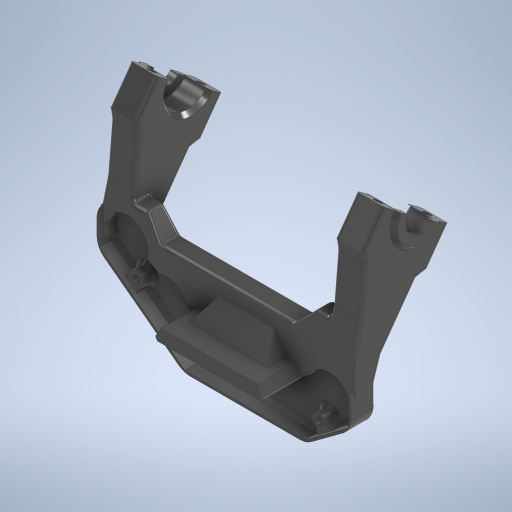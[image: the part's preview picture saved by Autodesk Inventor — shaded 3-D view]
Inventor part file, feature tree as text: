
AUTODESK INVENTOR PART (.ipt)
format: ipt  version: 2023.4 (Build 274418000, 418)  size: 1,474,048 bytes
history: native  units: mm
features: extrude x28, sketch x28, projected_geometry x26, chamfer x11, fillet x11, thicken_offset x4, mirror x1
ambient origin geometry x8: Origin, YZ Plane, XZ Plane, XY Plane, X Axis, Y Axis, Z Axis, Center Point
bodies: Solid1 (feature_tree)
feature tree (109):
  extrude  "Extrusion1"  Depth=10.0mm TaperAngle=0.0deg
  extrude  "Extrusion2"  Depth=6.0mm TaperAngle=0.0deg
  extrude  "Extrusion3"  Depth=4.3mm
  extrude  "Extrusion4"  Depth=4.3mm
  extrude  "Extrusion5"  Depth=10.0mm
  extrude  "Extrusion6"  Depth=7.2mm
  extrude  "Extrusion7"  Depth=3.3mm TaperAngle=0.0deg
  extrude  "Extrusion8"  Depth=10.0mm
  extrude  "Extrusion9"  Depth=2.0mm TaperAngle=45.0deg
  thicken_offset  "Thicken1"
  chamfer  "Chamfer1"  Distance=2.0mm Angle=45.0deg
  chamfer  "Chamfer2"  Distance=2.0mm Angle=45.0deg
  chamfer  "Chamfer3"  Distance=15.0mm
  thicken_offset  "Thicken2"
  mirror  "Mirror1"
  extrude  "Extrusion16"  Depth=15.0mm TaperAngle=0.0deg
  extrude  "Extrusion17"  Depth=10.0mm TaperAngle=0.0deg
  extrude  "Extrusion18"  TaperAngle=0.0deg  [1 undecoded]
  extrude  "Extrusion19"  TaperAngle=0.0deg  [1 undecoded]
  extrude  "Extrusion20"  Depth=10.0mm TaperAngle=0.0deg
  chamfer  "Chamfer7"  [1 undecoded]
  extrude  "Extrusion22"  Depth=4.3mm
  extrude  "Extrusion23"  Depth=4.3mm
  extrude  "Extrusion24"  Depth=7.5mm
  extrude  "Extrusion25"  Depth=7.5mm
  extrude  "Extrusion26"  Depth=3.5mm
  extrude  "Extrusion27"  Depth=7.5mm
  extrude  "Extrusion28"  Depth=15.0mm TaperAngle=0.0deg
  extrude  "Extrusion29"  Depth=10.0mm TaperAngle=0.0deg
  extrude  "Extrusion30"  Depth=2.0mm TaperAngle=45.0deg
  extrude  "Extrusion31"  Depth=2.0mm TaperAngle=45.0deg
  chamfer  "Chamfer8"  Distance=2.0mm
  chamfer  "Chamfer9"  Distance=2.0mm
  fillet  "Fillet1"  Radius=2.0mm
  fillet  "Fillet2"  Radius=2.0mm
  fillet  "Fillet3"  Radius=2.0mm
  fillet  "Fillet4"  Radius=2.0mm
  fillet  "Fillet5"  Radius=2.0mm
  fillet  "Fillet6"  Radius=2.0mm
  fillet  "Fillet7"  Radius=2.0mm
  fillet  "Fillet8"  Radius=2.0mm
  fillet  "Fillet9"  Radius=2.0mm
  fillet  "Fillet10"  Radius=16.0mm
  fillet  "Fillet11"  Radius=4.0mm
  extrude  "Extrusion32"  Depth=2.0mm TaperAngle=45.0deg
  chamfer  "Chamfer11"  Distance=4.0mm
  extrude  "Extrusion33"  Depth=2.0mm TaperAngle=45.0deg
  chamfer  "Chamfer12"  Distance=0.5mm
  extrude  "Extrusion34"  Depth=2.0mm TaperAngle=0.0deg
  extrude  "Extrusion36"  Depth=2.0mm TaperAngle=45.0deg
  chamfer  "Chamfer13"  Distance=5.0mm
  thicken_offset  "Thicken3"
  thicken_offset  "Thicken4"
  chamfer  "Chamfer14"  Distance=0.2mm
  chamfer  "Chamfer15"  Distance=0.2mm
  sketch  "Sketch1"  dims[d0=10.0mm d1=0.0mm d2=20.0mm d3=0.0mm]
  sketch  "Sketch2"  dims[d4=12.0mm d5=0.0mm d6=6.0mm d7=0.0mm]
  sketch  "Sketch5"  dims[d8=6.0mm d9=0.0mm d10=4.3mm]
  sketch  "Sketch6"  dims[d11=4.3mm d12=4.3mm]
  projected_geometry  "Projected Loop1"
  sketch  "Sketch7"  dims[d13=10.0mm d14=0.0mm d15=7.2mm]
  sketch  "Sketch8"  dims[d16=7.2mm d17=7.2mm]
  sketch  "Sketch9"  dims[d18=1.0mm d19=0.0mm d20=3.3mm d21=0.0mm]
  projected_geometry  "Projected Loop2"
  sketch  "Sketch10"  dims[d22=10.0mm d23=0.0mm d24=0.1mm]
  projected_geometry  "Projected Loop3"
  projected_geometry  "Projected Loop4"
  projected_geometry  "Projected Loop5"
  sketch  "Sketch11"  dims[d25=0.1mm d26=2.0mm d27=2.0mm d28=45.0deg d29=2.0mm d30=2.0mm d31=45.0deg d32=2.0mm d33=2.0mm d34=45.0deg]
  sketch  "Sketch18"  dims[d38=0.1mm]
  sketch  "Sketch19"  dims[d39=0.1mm]
  sketch  "Sketch20"  dims[d58=32.0mm]
  projected_geometry  "Projected Loop8"
  projected_geometry  "Projected Loop9"
  sketch  "Sketch21"  dims[d59=110.0mm]
  sketch  "Sketch22"  dims[d60=40.0mm d61=15.0mm d62=0.0mm]
  projected_geometry  "Projected Loop10"
  projected_geometry  "Projected Loop11"
  sketch  "Sketch24"  dims[d63=15.0mm d64=0.0mm d65=15.0mm d66=0.0mm]
  projected_geometry  "Projected Loop12"
  sketch  "Sketch25"  dims[d67=15.0mm d68=0.0mm d69=10.0mm d70=0.0mm]
  projected_geometry  "Projected Loop13"
  sketch  "Sketch26"  dims[d71=6.0mm d72=2.0mm d73=45.0deg d77=0.0mm d78=0.0mm]
  projected_geometry  "Projected Loop14"
  sketch  "Sketch27"  dims[d79=10.0mm d80=0.0mm d81=0.0mm d82=0.0mm]
  sketch  "Sketch28"  dims[d83=10.0mm d84=0.0mm d85=10.0mm d86=0.0mm]
  projected_geometry  "Projected Loop15"
  projected_geometry  "Projected Loop16"
  sketch  "Sketch29"  dims[d87=25.0mm d88=0.0mm d89=0.0mm]
  sketch  "Sketch30"  dims[d90=4.3mm d91=4.3mm]
  sketch  "Sketch32"  dims[d92=4.3mm d93=4.3mm]
  projected_geometry  "Projected Loop17"
  projected_geometry  "Projected Loop18"
  projected_geometry  "Projected Loop19"
  projected_geometry  "Projected Loop20"
  sketch  "Sketch33"  dims[d94=3.5mm d95=7.5mm]
  projected_geometry  "Projected Loop21"
  projected_geometry  "Projected Loop22"
  sketch  "Sketch34"  dims[d96=3.5mm d97=7.5mm]
  projected_geometry  "Projected Loop23"
  projected_geometry  "Projected Loop24"
  sketch  "Sketch35"  dims[d98=3.5mm d99=3.5mm]
  projected_geometry  "Projected Loop25"
  sketch  "Sketch36"  dims[d100=7.5mm d101=7.5mm]
  projected_geometry  "Projected Loop26"
  sketch  "Sketch37"  dims[d102=15.0mm d103=0.0mm d104=15.0mm d105=0.0mm]
  sketch  "Sketch39"  dims[d106=15.0mm d107=0.0mm d108=10.0mm d109=0.0mm d110=4.065mm d111=2.0mm d112=45.0deg d113=4.047mm d114=2.0mm d115=45.0deg d116=2.0mm d117=2.0mm d118=2.0mm d119=2.0mm d120=2.0mm d121=2.0mm d122=2.0mm d123=2.0mm d124=2.0mm d125=2.0mm d126=2.0mm d130=16.0mm d131=4.0mm d132=0.0mm d133=2.0mm d134=2.0mm d135=45.0deg d136=4.0mm d137=0.0mm d138=2.0mm d139=2.0mm d140=45.0deg d141=0.5mm d142=0.0mm d149=5.0mm d150=0.0mm d151=5.0mm d152=2.0mm d153=45.0deg d154=5.0mm d155=0.2mm d156=0.2mm d157=0.2mm d158=0.2mm d159=2.0mm d160=2.0mm d161=45.0deg d162=1.0mm d163=2.0mm d164=45.0deg d56=0.5mm d57=0.872665mm]
  projected_geometry  "Projected Loop27"
  projected_geometry  "Projected Loop28"
note: 3 required parameter values undecoded (feature->parameter linkage not recoverable at this tier; creation-order binding heuristic only, values carry confidence <= 0.55)
